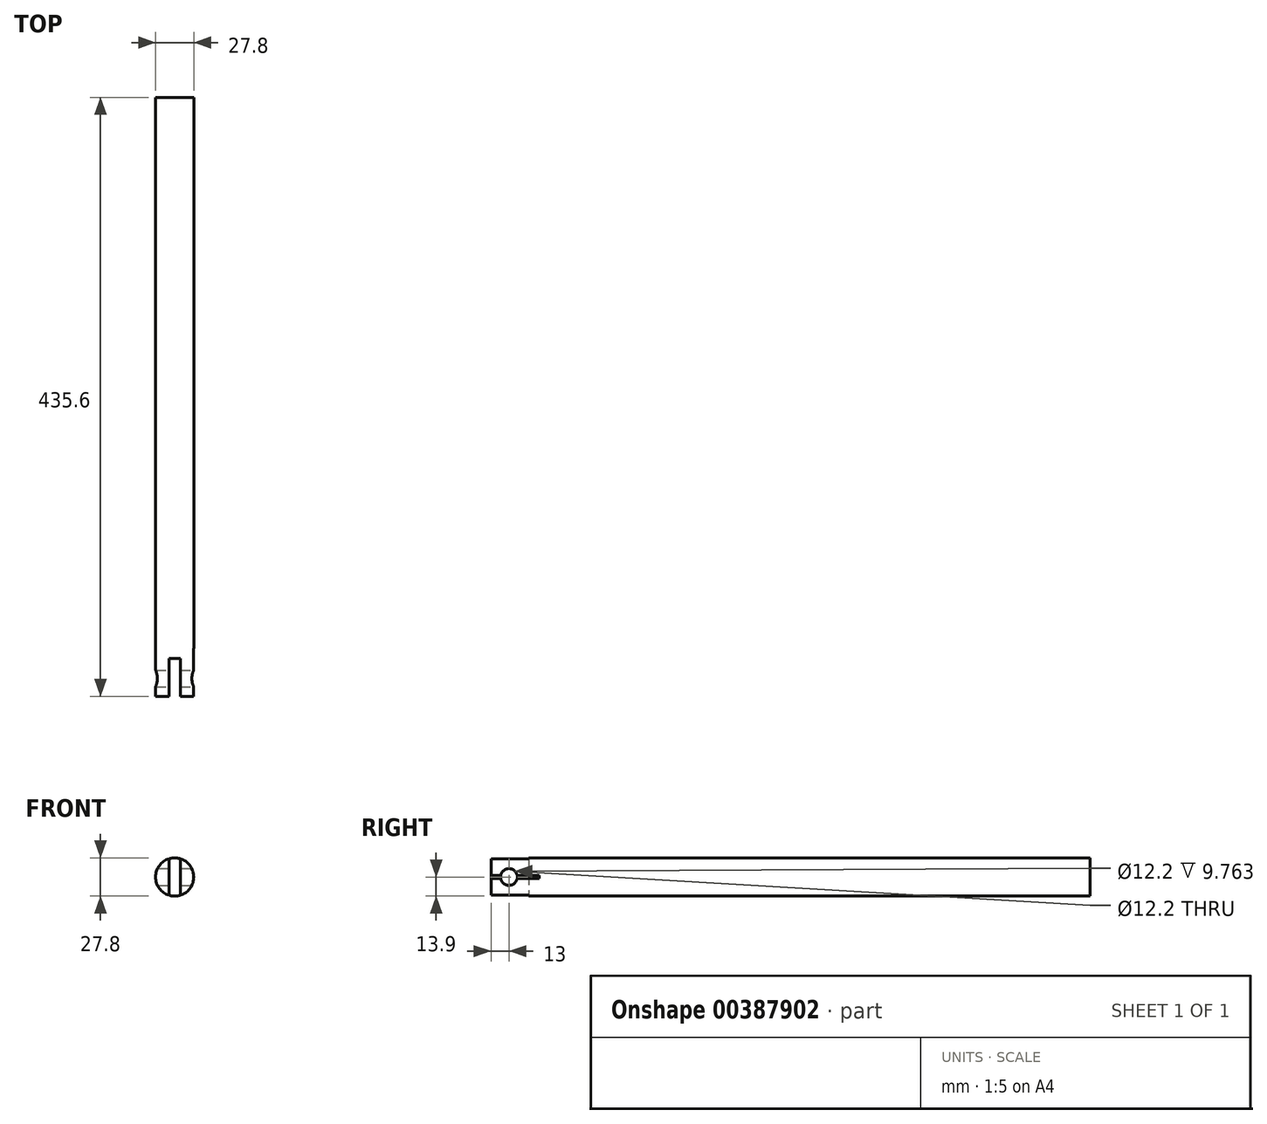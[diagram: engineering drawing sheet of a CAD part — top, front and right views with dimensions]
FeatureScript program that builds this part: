
annotation { "Feature Type Name" : "Feature", "Feature Type Description" : "" }
export const myFeature = defineFeature(function(context is Context, id is Id, definition is map)
    precondition{}
    {
        {
            var Q0;
            Q0=qCreatedBy(makeId("Front.planeOp"),FACE);
            var sketch = newSketch(context, id + "F0", { "sketchPlane" : qUnion([Q0])});
            skCircle(sketch, "E0", {"center": v(0, 0) * mm, "radius": 13.9 * mm});
            skSolve(sketch);
        }
        {
            var Q0;
            Q0=qSketchRegion(id+"F0",true);
            extrude(context, id + "F1", {"entities" : qUnion([Q0]), "depth" : 435.6 * mm, "symmetric" : true});
        }
        {
            var Q0;
            Q0=makeQuery(id+"F1.opExtrude","CAP_FACE",FACE,{"disambiguationData":[OSD([sQuery(id+"F0.wireOp",EDGE,"E0")])],"isStart":false});
            var sketch = newSketch(context, id + "F2", { "sketchPlane" : qUnion([Q0])});
            skLineSegment(sketch, "E1.left", {"start": v(-13.86, 1.02) * mm, "end": v(-13.86, -1.02) * mm});
            skLineSegment(sketch, "E1.right", {"start": v(13.86, 1.02) * mm, "end": v(13.86, -1.02) * mm});
            skPoint(sketch, "E1.middle", {"position": v(0, 0) * mm});
            skSolve(sketch);
        }
        {
            var Q0;
            {var subQ0=sQuery(id+"F2.wireOp",EDGE,"E1.right");Q0=makeQuery(id+"F2.imprint","IMPRINT",FACE,{"disambiguationData":[TD([[makeQuery(id+"F2.imprint","IMPRINT",EDGE,{"derivedFrom":subQ0}),1.0]])]});}
            extrude(context, id + "F3", {"entities" : qUnion([Q0]), "operationType" : NewBodyOperationType.REMOVE, "oppositeDirection" : true, "depth" : 35 * mm});
        }
        {
            var Q0;
            Q0=makeQuery(id+"F3.boolean.opBoolean","COPY",FACE,{"derivedFrom":makeQuery(id+"F3.opExtrude","SWEPT_FACE",FACE,{"disambiguationData":[OSD([sQuery(id+"F2.wireOp",EDGE,"E1.right")])]})});
            var sketch = newSketch(context, id + "F4", { "sketchPlane" : qUnion([Q0])});
            skLineSegment(sketch, "E2", {"start": v(-204.8, 0) * mm, "end": v(-217.8, 0) * mm});
            skPoint(sketch, "E2.startSnap0", {"position": v(-217.8, 0) * mm});
            skSolve(sketch);
        }
        {
            var Q0;
            Q0=sQuery(id+"F4.wireOp",VERTEX,"E2.start");
            var Q1;
            Q1=makeQuery(id+"F1.opExtrude","SWEPT_BODY",BODY,{"disambiguationData":[OSD([sQuery(id+"F0.wireOp",EDGE,"E0")])]});
            hole(context, id + "F5", {"style" : HoleStyle.SIMPLE, "endStyle" : HoleEndStyle.THROUGH, "holeDiameter" : 12.2 * mm, "isTappedThrough" : true, "tappedDepth" : 12 * mm, "tapClearance" : 3, "locations" : qUnion([Q0]), "scope" : qUnion([Q1])});
        }
        {
            var Q0;
            Q0=makeQuery(id+"F1.opExtrude","CAP_FACE",FACE,{"disambiguationData":[OSD([sQuery(id+"F0.wireOp",EDGE,"E0")])],"isStart":false});
            var sketch = newSketch(context, id + "F6", { "sketchPlane" : qUnion([Q0])});
            skLineSegment(sketch, "E3.bottom", {"start": v(-4.1, 39.9) * mm, "end": v(4.1, 39.9) * mm});
            skLineSegment(sketch, "E3.top", {"start": v(-4.1, -39.9) * mm, "end": v(4.1, -39.9) * mm});
            skLineSegment(sketch, "E3.left", {"start": v(-4.1, 39.9) * mm, "end": v(-4.1, -39.9) * mm});
            skLineSegment(sketch, "E3.right", {"start": v(4.1, 39.9) * mm, "end": v(4.1, -39.9) * mm});
            skPoint(sketch, "E3.middle", {"position": v(0, 0) * mm});
            skSolve(sketch);
        }
        {
            var Q0;
            {var subQ0=sQuery(id+"F6.wireOp",EDGE,"E3.left");var subQ1=makeQuery(id+"F1.opExtrude","CAP_EDGE",EDGE,{"disambiguationData":[OSD([sQuery(id+"F0.wireOp",EDGE,"E0")])],"isStart":false});var subQ2=makeQuery(id+"F6.imprint","INTERSECT",VERTEX,{"disambiguationData":[OD(0.0)],"derivedFrom":[subQ1,subQ0]});Q0=makeQuery(id+"F6.imprint","IMPRINT",FACE,{"disambiguationData":[TD([[makeQuery(id+"F6.imprint","IMPRINT",EDGE,{"disambiguationData":[TD([[subQ2,-1.0]])],"derivedFrom":subQ0}),1.0]])]});}
            extrude(context, id + "F7", {"entities" : qUnion([Q0]), "operationType" : NewBodyOperationType.REMOVE, "oppositeDirection" : true, "depth" : 27.5 * mm});
        }
    });
